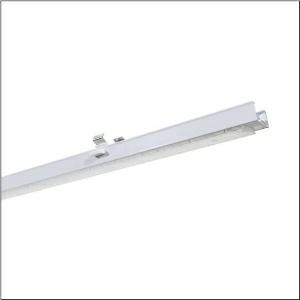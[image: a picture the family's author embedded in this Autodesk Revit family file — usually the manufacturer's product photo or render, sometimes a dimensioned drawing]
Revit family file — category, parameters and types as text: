
# Revit family: sanierungs-leuchteneinsatz_31_gen_2_51re18mb48b_28b9
name_source: partatom
category: Lighting Fixtures
units: mm (PartAtom-declared; Revit-internal decimal feet)

## family parameters
Cut with Voids When Loaded = No
Host = Face
Light Source = No
Part Type = Normal
Room Calculation Point = No
Round Connector Dimension = Use Diameter
Shared = No

## types (1)
- --- (1 x LED, 8000 lm, 50 W, 4000K)
    Apparent Load = 50 VA
    CIE Flux Codes = 71 89 97 97 100
    Color Rendering = 80
    Color Temperature = 4000K
    Default Elevation = 1800 mm
    Description = Refurbishment luminaire insert Gen.2, luminaire insert, of extruded aluminium section, coated, traffic white (RAL 9016), length: 1.472mm, width: 91mm, height: 53mm, LED rated luminous flux: 8.000lm, light colour: 840, control gear: ON/OFF Multilumen, control gear: ECG Multilumen, with system connector: socket, mains connection: 220..240V, AC/DC, 0/50..60Hz, luminous flux adjustable on luminaire in four steps (4280/5650/6950/8270lm), connected load according to luminous flux setting (24/32/40/49W), primary light control with lens, of plastic, primary optical cover: cover, of PMMA, light emission: direct distribution, protection rating (complete): IP20, insulation class (complete): insulation class I (protective earthing), certification: CE, UKCA, permissible ambient temperature for indoor applications: -20..+40°C, packaging unit: 1 piece
    Height = 58 mm
    Lamp = 1 x LED
    Lamp Light Flux = 8000 lm
    Lamp Power = 50 W
    Lamp count = 1
    Length = 1472 mm
    Luminous efficacy = 160 lm/W
    Manufacturer = Siteco
    ModVariant = No
    Model = 51RE18MB48B
    Mounting Place = Ceiling
    Mounting Type = Pendant
    Number of Poles = 1
    OnlyDefault = Yes
    Power Factor = 1
    Product Name = Sanierungs-Leuchteneinsatz 31 Gen.2
    Product group = luminaire insert
    ProductGroupID = 902
    Protection Class = Protection class I
    Protection Degree = IP 20
    RLX_Detail_Level = 1
    RlxData = <blob elided: 20457 chars, md5=e62e9197>
    Socket = socket
    Standby Power = 0 W
    System Light Flux = 8000 lm
    System Power = 50 W
    Type Comments = factory setting: luminous flux: 100 % | (ON | ON) | 300 mA
    Type Image = l_1266702.jpg
    URL = http://relux.com
    VarID = @adj_089629
    Voltage = 0 V
    Weight = 0.00 kg
    Width = 65 mm

## geometry (parser evidence)
native form markers: Blend x4, Sweep x12
no freeform markers — native parametric forms only
